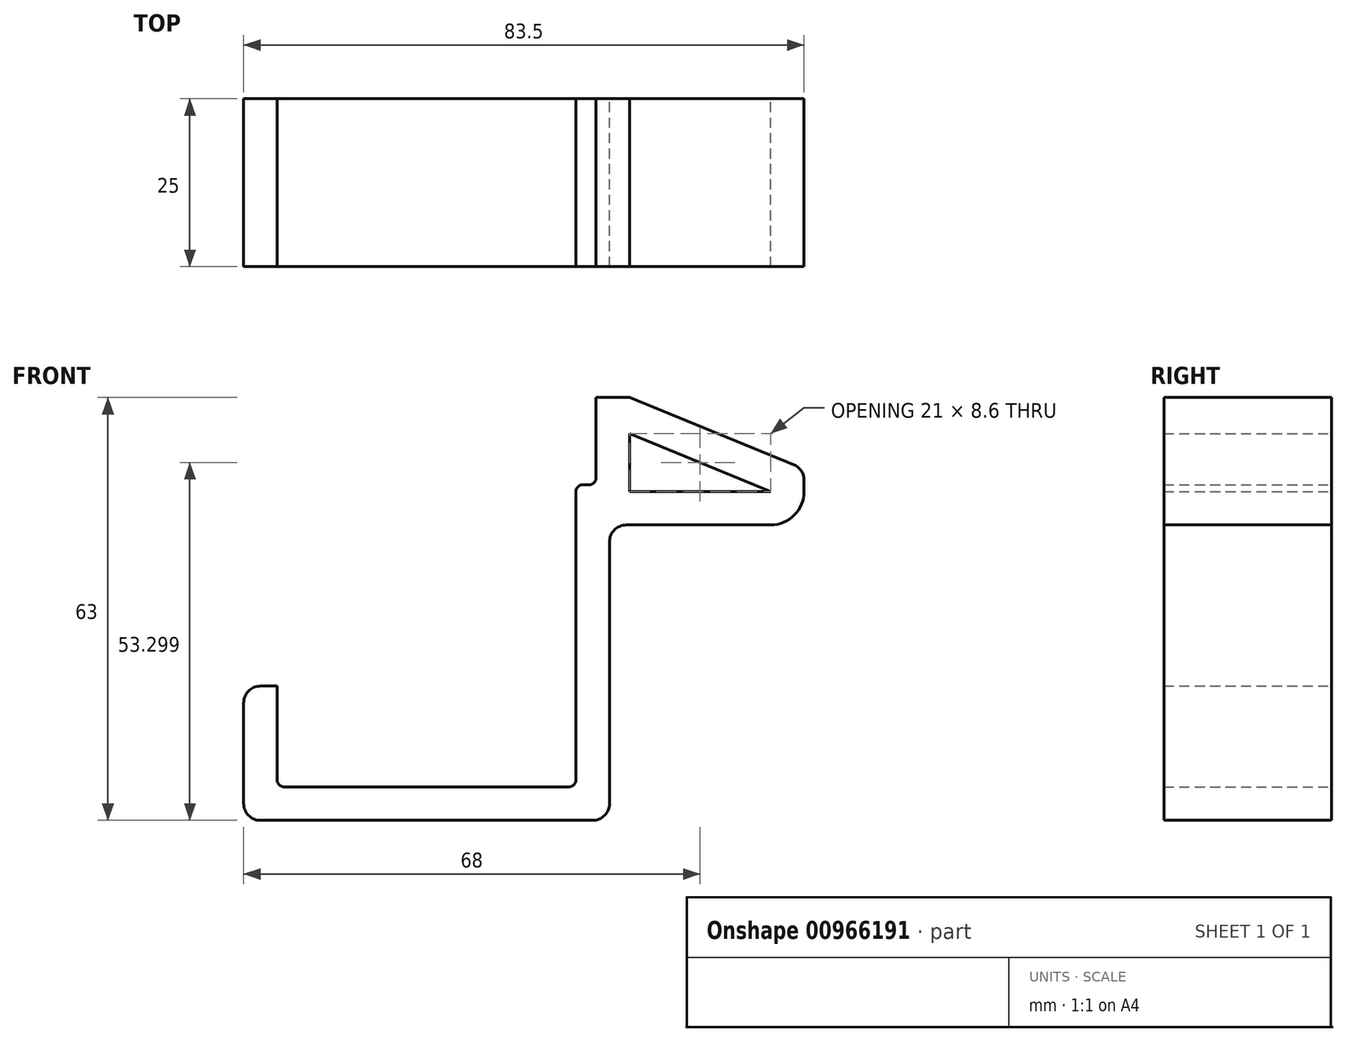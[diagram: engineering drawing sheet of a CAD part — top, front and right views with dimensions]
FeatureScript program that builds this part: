
annotation { "Feature Type Name" : "Feature", "Feature Type Description" : "" }
export const myFeature = defineFeature(function(context is Context, id is Id, definition is map)
    precondition{}
    {
        {
            var Q0;
            Q0=qCreatedBy(makeId("Front.planeOp"),FACE);
            var sketch = newSketch(context, id + "F0", { "sketchPlane" : qUnion([Q0])});
            skLineSegment(sketch, "E0.bottom", {"start": v(-44.5, 0) * mm, "end": v(0, 0) * mm});
            skLineSegment(sketch, "E0.top", {"start": v(-44.5, -5) * mm, "end": v(0, -5) * mm});
            skLineSegment(sketch, "E1.bottom", {"start": v(-44.5, -5) * mm, "end": v(-49.5, -5) * mm});
            skLineSegment(sketch, "E1.top", {"start": v(-44.5, 15) * mm, "end": v(-49.5, 15) * mm});
            skLineSegment(sketch, "E1.left", {"start": v(-44.5, 0) * mm, "end": v(-44.5, 15) * mm});
            skLineSegment(sketch, "E1.right", {"start": v(-49.5, -5) * mm, "end": v(-49.5, 15) * mm});
            skLineSegment(sketch, "E2.bottom", {"start": v(0, -5) * mm, "end": v(5, -5) * mm});
            skLineSegment(sketch, "E2.top", {"start": v(0, 45) * mm, "end": v(3, 45) * mm});
            skLineSegment(sketch, "E2.left", {"start": v(0, 0) * mm, "end": v(0, 45) * mm});
            skLineSegment(sketch, "E2.right", {"start": v(5, -5) * mm, "end": v(5, 39) * mm});
            skLineSegment(sketch, "E3.bottom", {"start": v(5, 39) * mm, "end": v(34, 39) * mm});
            skLineSegment(sketch, "E3.top", {"start": v(3, 58) * mm, "end": v(8, 58) * mm});
            skLineSegment(sketch, "E3.right", {"start": v(34, 39) * mm, "end": v(34, 47.36) * mm});
            skLineSegment(sketch, "E4", {"start": v(8, 58) * mm, "end": v(34, 47.36) * mm});
            skLineSegment(sketch, "E5", {"start": v(3, 58) * mm, "end": v(3, 45) * mm});
            skLineSegment(sketch, "E6", {"start": v(8, 44) * mm, "end": v(29, 44) * mm});
            skLineSegment(sketch, "E7", {"start": v(29, 44) * mm, "end": v(8, 52.6) * mm});
            skLineSegment(sketch, "E8", {"start": v(8, 52.6) * mm, "end": v(8, 44) * mm});
            skSolve(sketch);
        }
        {
            var Q0;
            Q0 = qSketchRegion(id + "F0", true);
            extrude(context, id + "F1", {"entities" : qUnion([Q0]), "endBound" : BoundingType.SYMMETRIC, "depth" : 25 * mm, "offsetDistance" : 25 * mm});
        }
        {
            var Q0;
            Q0=makeQuery(id+"F1.opExtrude","SWEPT_EDGE",EDGE,{"disambiguationData":[OSD([sQuery(id+"F0.wireOp",EDGE,"E3.bottom"),sQuery(id+"F0.wireOp",EDGE,"E3.right")])]});
            fillet(context, id + "F2", {"entities" : qUnion([Q0]), "radius" : 5 * mm, "tangentPropagation" : true, "allowEdgeOverflow" : false});
        }
        {
            var Q0;
            Q0=makeQuery(id+"F1.opExtrude","SWEPT_EDGE",EDGE,{"disambiguationData":[OSD([sQuery(id+"F0.wireOp",EDGE,"E2.bottom"),sQuery(id+"F0.wireOp",EDGE,"E2.right")])]});
            var Q1;
            Q1=makeQuery(id+"F1.opExtrude","SWEPT_EDGE",EDGE,{"disambiguationData":[OSD([sQuery(id+"F0.wireOp",EDGE,"E1.bottom"),sQuery(id+"F0.wireOp",EDGE,"E1.right")])]});
            var Q2;
            Q2=makeQuery(id+"F1.opExtrude","SWEPT_EDGE",EDGE,{"disambiguationData":[OSD([sQuery(id+"F0.wireOp",EDGE,"E1.top"),sQuery(id+"F0.wireOp",EDGE,"E1.right")])]});
            var Q3;
            Q3=makeQuery(id+"F1.opExtrude","SWEPT_EDGE",EDGE,{"disambiguationData":[OSD([sQuery(id+"F0.wireOp",EDGE,"E3.right"),sQuery(id+"F0.wireOp",EDGE,"E4")])]});
            var Q4;
            Q4=makeQuery(id+"F1.opExtrude","SWEPT_EDGE",EDGE,{"disambiguationData":[OSD([sQuery(id+"F0.wireOp",EDGE,"E2.right"),sQuery(id+"F0.wireOp",EDGE,"E3.bottom")])]});
            fillet(context, id + "F3", {"entities" : qUnion([Q0, Q1, Q2, Q3, Q4]), "radius" : 2.5 * mm, "tangentPropagation" : true, "allowEdgeOverflow" : false});
        }
        {
            var Q0;
            Q0=makeQuery(id+"F1.opExtrude","SWEPT_EDGE",EDGE,{"disambiguationData":[OSD([sQuery(id+"F0.wireOp",EDGE,"E2.top"),sQuery(id+"F0.wireOp",EDGE,"E5")])]});
            var Q1;
            Q1=makeQuery(id+"F1.opExtrude","SWEPT_EDGE",EDGE,{"disambiguationData":[OSD([sQuery(id+"F0.wireOp",EDGE,"E2.top"),sQuery(id+"F0.wireOp",EDGE,"E2.left")])]});
            var Q2;
            Q2=makeQuery(id+"F1.opExtrude","SWEPT_EDGE",EDGE,{"disambiguationData":[OSD([sQuery(id+"F0.wireOp",EDGE,"E0.bottom"),sQuery(id+"F0.wireOp",EDGE,"E2.left")])]});
            var Q3;
            Q3=makeQuery(id+"F1.opExtrude","SWEPT_EDGE",EDGE,{"disambiguationData":[OSD([sQuery(id+"F0.wireOp",EDGE,"E0.bottom"),sQuery(id+"F0.wireOp",EDGE,"E1.left")])]});
            fillet(context, id + "F4", {"entities" : qUnion([Q0, Q1, Q2, Q3]), "radius" : 1 * mm, "tangentPropagation" : true, "allowEdgeOverflow" : false});
        }
    });
